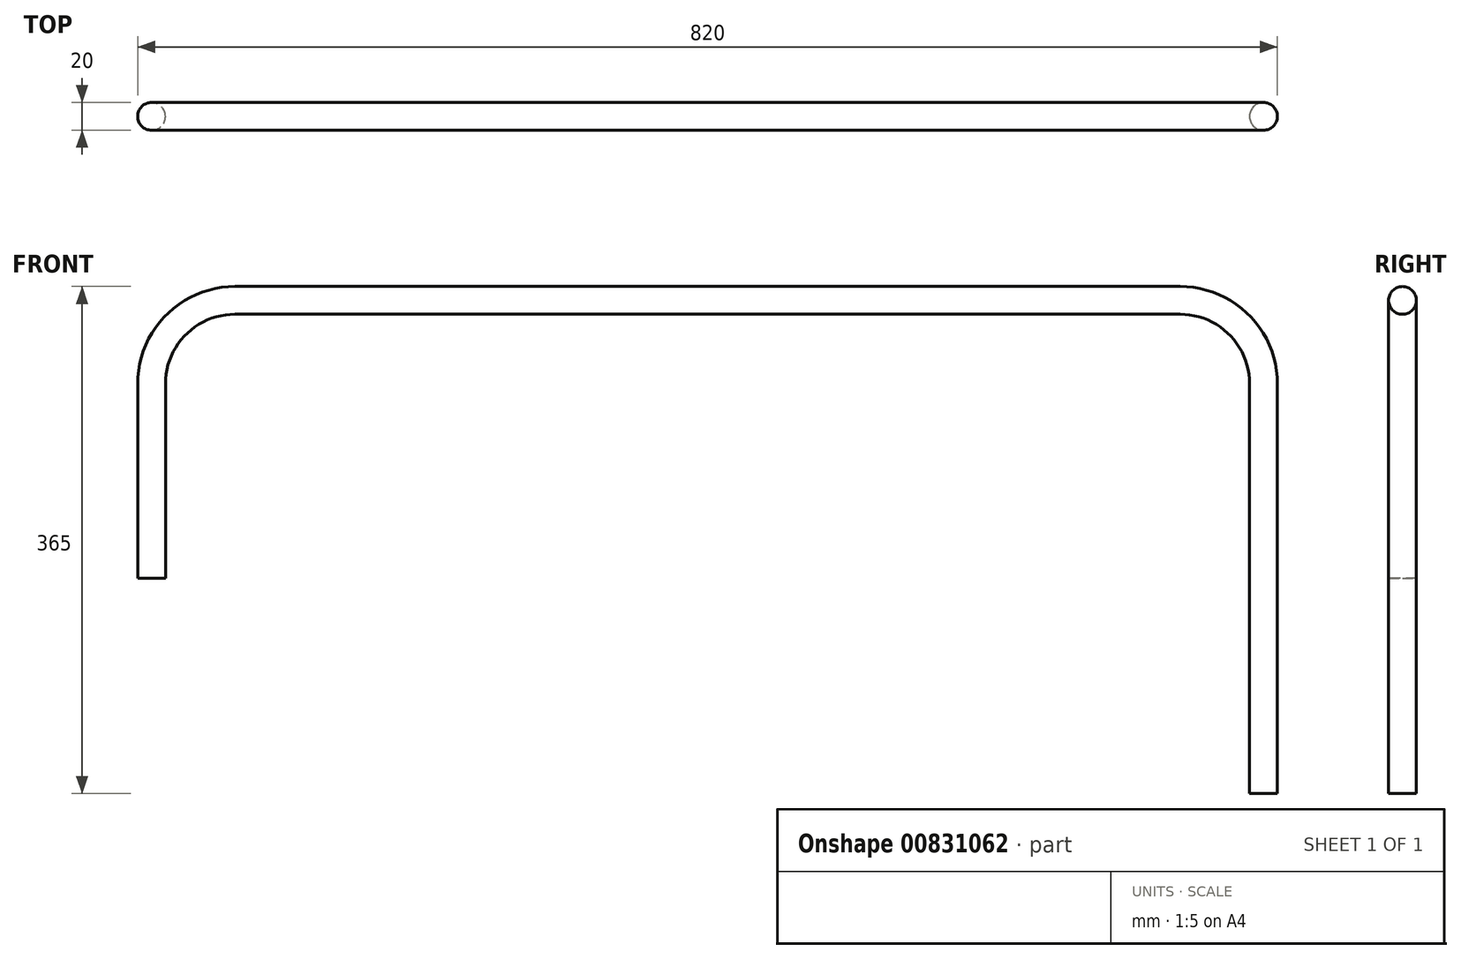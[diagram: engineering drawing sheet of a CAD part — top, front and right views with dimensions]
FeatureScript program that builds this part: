
annotation { "Feature Type Name" : "Feature", "Feature Type Description" : "" }
export const myFeature = defineFeature(function(context is Context, id is Id, definition is map)
    precondition{}
    {
        {
            var Q0;
            Q0=qCreatedBy(makeId("Front.planeOp"),FACE);
            var sketch = newSketch(context, id + "F0", { "sketchPlane" : qUnion([Q0])});
            skLineSegment(sketch, "E0", {"start": v(0, 0) * mm, "end": v(0, 140) * mm});
            skLineSegment(sketch, "E1", {"start": v(60, 200) * mm, "end": v(740, 200) * mm});
            skLineSegment(sketch, "E2", {"start": v(800, 140) * mm, "end": v(800, -155) * mm});
            skPoint(sketch, "E3.visualSharp", {"position": v(0, 200) * mm});
            skArc(sketch, "E3.filletArc", {"start": v(60, 200) * mm, "mid": v(17.57, 182.43) * mm, "end": v(0, 140) * mm});
            skPoint(sketch, "E4.visualSharp", {"position": v(800, 200) * mm});
            skArc(sketch, "E4.filletArc", {"start": v(800, 140) * mm, "mid": v(782.43, 182.43) * mm, "end": v(740, 200) * mm});
            skSolve(sketch);
        }
        {
            var Q0;
            Q0=qCreatedBy(makeId("Top.planeOp"),FACE);
            var sketch = newSketch(context, id + "F1", { "sketchPlane" : qUnion([Q0])});
            skCircle(sketch, "E5", {"center": v(0, 0) * mm, "radius": 10 * mm});
            skSolve(sketch);
        }
        {
            var Q0;
            Q0=makeQuery(id+"F1.imprint","IMPRINT",FACE,{"disambiguationData":[TD([[makeQuery(id+"F1.imprint","IMPRINT",EDGE,{"derivedFrom":sQuery(id+"F1.wireOp",EDGE,"E5")}),1.0]])]});
            var Q1;
            Q1=sQuery(id+"F0.wireOp",EDGE,"E0");
            var Q2;
            Q2=sQuery(id+"F0.wireOp",EDGE,"E3.filletArc");
            var Q3;
            Q3=sQuery(id+"F0.wireOp",EDGE,"E1");
            var Q4;
            Q4=sQuery(id+"F0.wireOp",EDGE,"E4.filletArc");
            var Q5;
            Q5=sQuery(id+"F0.wireOp",EDGE,"E2");
            sweep(context, id + "F2", {"profiles" : qUnion([Q0]), "path" : qUnion([Q1, Q2, Q3, Q4, Q5])});
        }
    });
